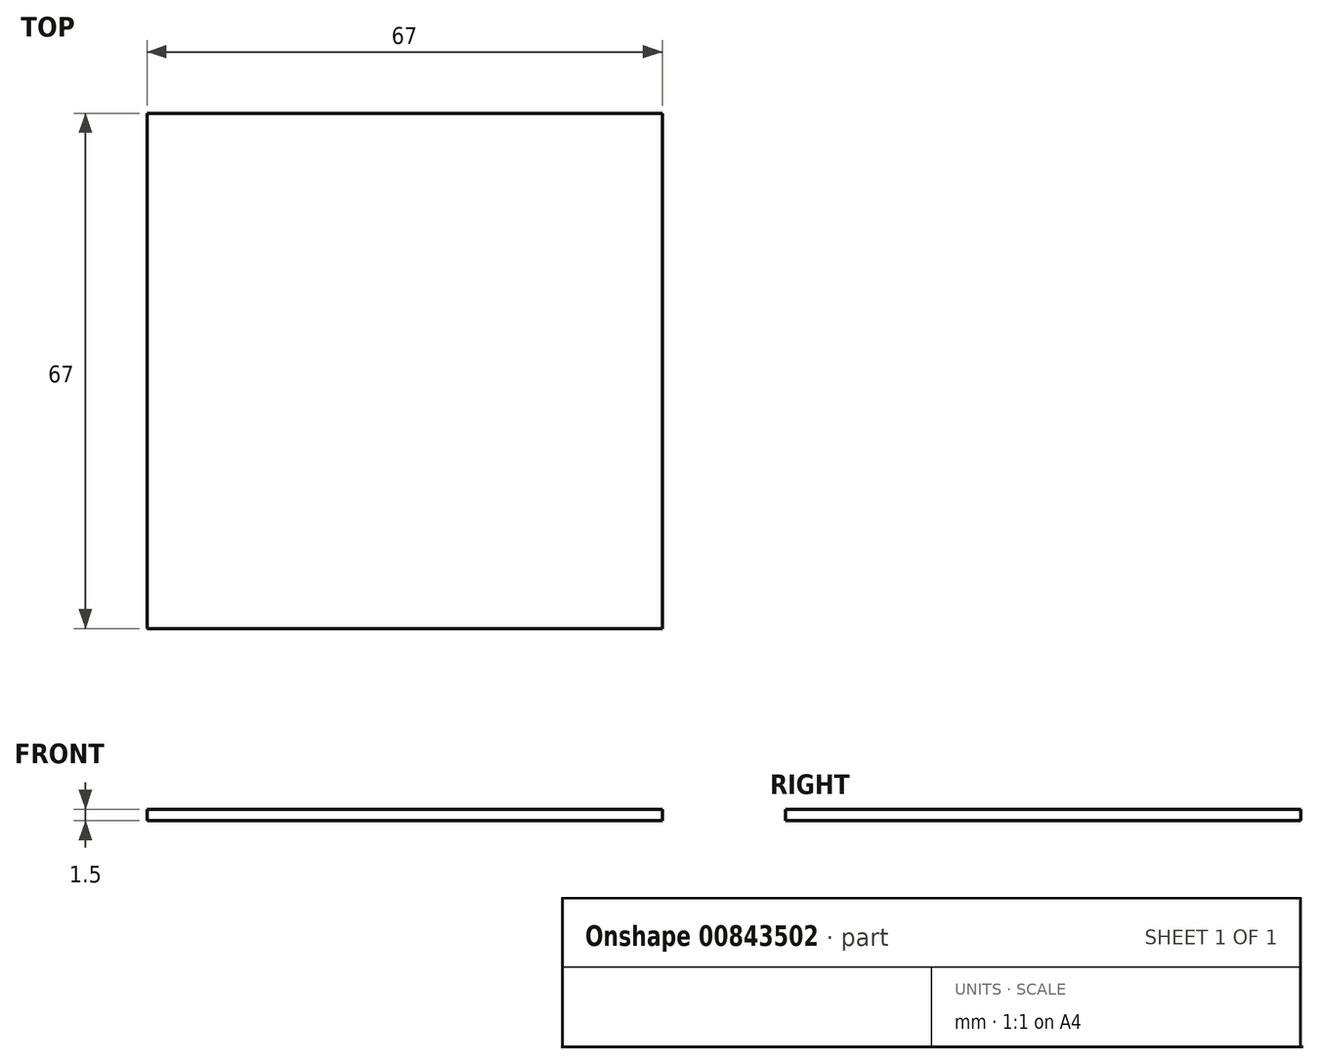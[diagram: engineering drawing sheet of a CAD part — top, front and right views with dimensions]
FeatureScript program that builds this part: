
annotation { "Feature Type Name" : "Feature", "Feature Type Description" : "" }
export const myFeature = defineFeature(function(context is Context, id is Id, definition is map)
    precondition{}
    {
        {
            var Q0;
            Q0=qCreatedBy(makeId("Top.planeOp"),FACE);
            var sketch = newSketch(context, id + "F0", { "sketchPlane" : qUnion([Q0])});
            skLineSegment(sketch, "E0.bottom", {"start": v(0, 0) * mm, "end": v(-67, 0) * mm});
            skLineSegment(sketch, "E0.top", {"start": v(0, 67) * mm, "end": v(-67, 67) * mm});
            skLineSegment(sketch, "E0.left", {"start": v(0, 0) * mm, "end": v(0, 67) * mm});
            skLineSegment(sketch, "E0.right", {"start": v(-67, 0) * mm, "end": v(-67, 67) * mm});
            skSolve(sketch);
        }
        {
            var Q0;
            Q0 = qSketchRegion(id + "F0", true);
            extrude(context, id + "F1", {"entities" : qUnion([Q0]), "depth" : 1.5 * mm, "offsetDistance" : 25 * mm});
        }
    });
